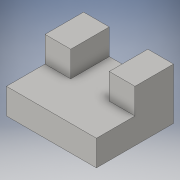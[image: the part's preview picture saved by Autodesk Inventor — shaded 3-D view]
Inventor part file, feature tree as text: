
AUTODESK INVENTOR PART (.ipt)
format: ipt  version: 2016 (Build 200138000, 138)  size: 111,616 bytes
history: native  units: in
note: dims shown in document units (in); Inventor stores cm internally (conversion verified against a paired STEP export)
features: extrude x3, sketch x3
ambient origin geometry x8: Origin, YZ Plane, XZ Plane, XY Plane, X Axis, Y Axis, Z Axis, Center Point
bodies: Solid1 (feature_tree)
feature tree (6):
  extrude  "Extrusion1"  Depth=1.0in
  extrude  "Extrusion2"  Depth=0.75in
  extrude  "Extrusion3"  Depth=0.5in
  sketch  "Sketch1"  dims[d0=1.75in d1=1.0in]
  sketch  "Sketch2"  dims[d2=1.5in d3=0.0in d4=0.75in]
  sketch  "Sketch3"  dims[d5=0.5in d6=0.0in d7=0.5in d8=0.5in d9=0.75in d10=0.5in d11=0.0in]
